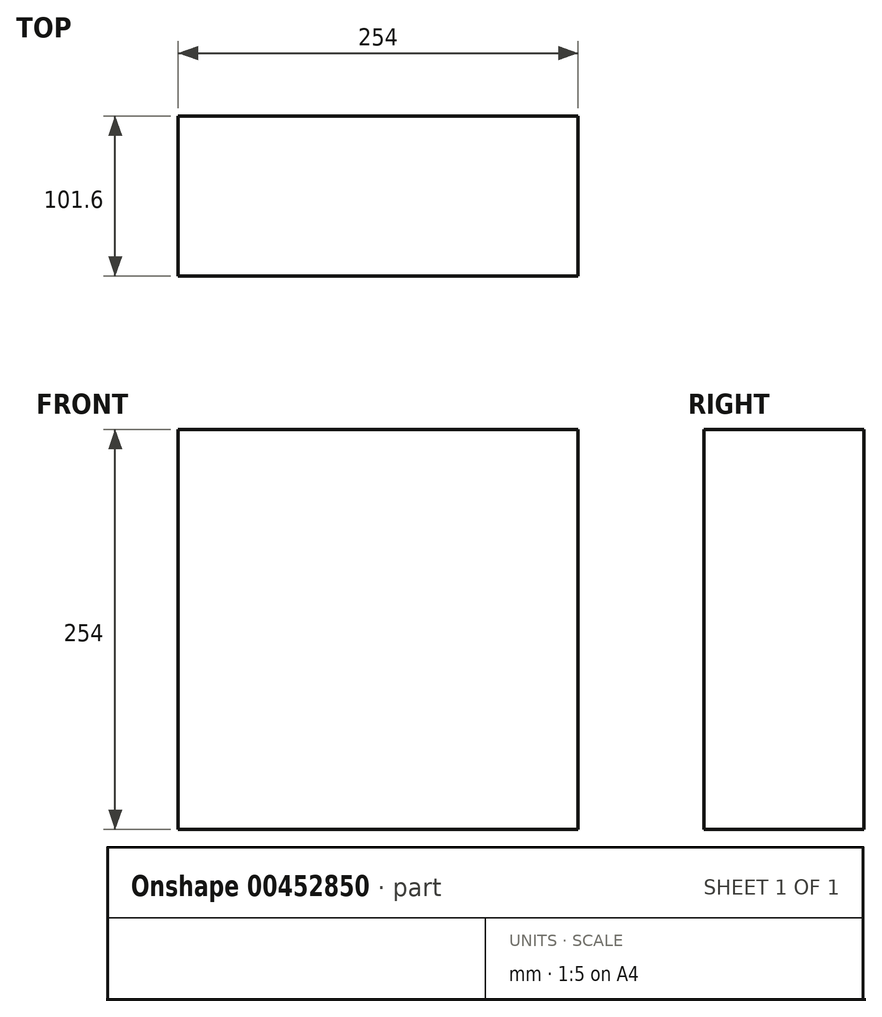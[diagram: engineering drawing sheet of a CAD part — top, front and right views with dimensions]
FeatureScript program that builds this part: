
annotation { "Feature Type Name" : "Feature", "Feature Type Description" : "" }
export const myFeature = defineFeature(function(context is Context, id is Id, definition is map)
    precondition{}
    {
        {
            var Q0;
            Q0=qCreatedBy(makeId("Top.planeOp"),FACE);
            var sketch = newSketch(context, id + "F0", { "sketchPlane" : qUnion([Q0])});
            skLineSegment(sketch, "E0.bottom", {"start": v(127, 50.8) * mm, "end": v(-127, 50.8) * mm});
            skLineSegment(sketch, "E0.top", {"start": v(127, -50.8) * mm, "end": v(-127, -50.8) * mm});
            skLineSegment(sketch, "E0.left", {"start": v(127, 50.8) * mm, "end": v(127, -50.8) * mm});
            skLineSegment(sketch, "E0.right", {"start": v(-127, 50.8) * mm, "end": v(-127, -50.8) * mm});
            skPoint(sketch, "E0.middle", {"position": v(0, 0) * mm});
            skSolve(sketch);
        }
        {
            var Q0;
            Q0 = qSketchRegion(id + "F0", true);
            extrude(context, id + "F1", {"entities" : qUnion([Q0]), "depth" : 254 * mm});
        }
    });
